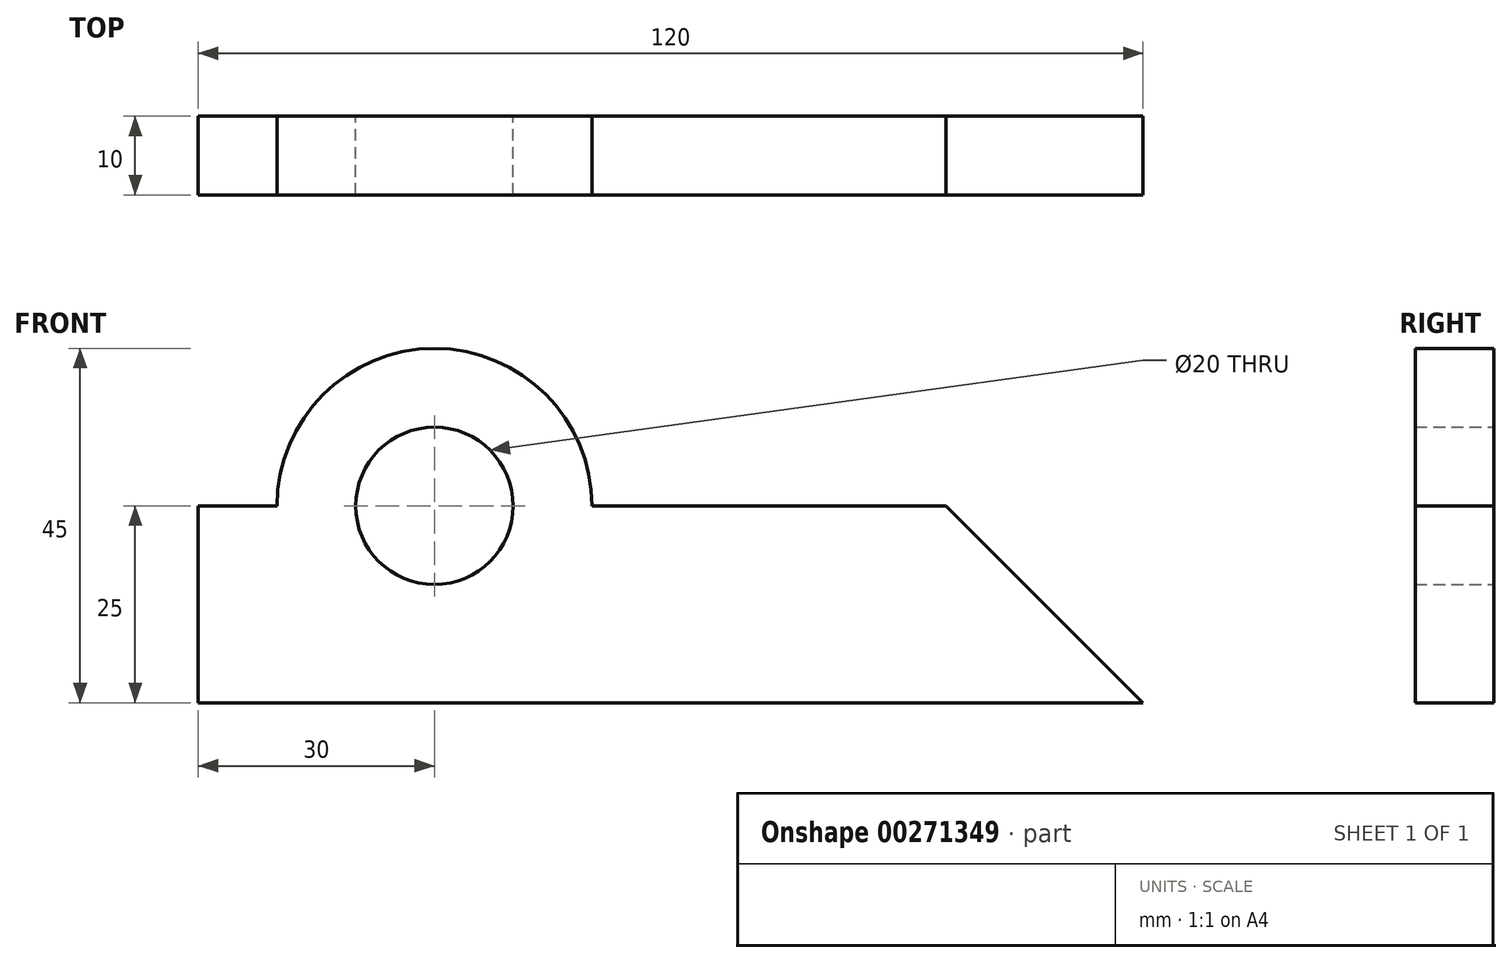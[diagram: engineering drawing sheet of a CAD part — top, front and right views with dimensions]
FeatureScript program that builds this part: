
annotation { "Feature Type Name" : "Feature", "Feature Type Description" : "" }
export const myFeature = defineFeature(function(context is Context, id is Id, definition is map)
    precondition{}
    {
        {
            var Q0;
            Q0=qCreatedBy(makeId("Front.planeOp"),FACE);
            var sketch = newSketch(context, id + "F0", { "sketchPlane" : qUnion([Q0])});
            skLineSegment(sketch, "E0", {"start": v(0, 0) * mm, "end": v(0, 25) * mm});
            skLineSegment(sketch, "E1", {"start": v(0, 25) * mm, "end": v(10, 25) * mm});
            skLineSegment(sketch, "E2", {"start": v(0, 0) * mm, "end": v(120, 0) * mm});
            skLineSegment(sketch, "E3", {"start": v(120, 0) * mm, "end": v(95, 25) * mm});
            skLineSegment(sketch, "E4", {"start": v(95, 25) * mm, "end": v(50, 25) * mm});
            skCircle(sketch, "E5", {"center": v(30, 25) * mm, "radius": 10 * mm});
            skArc(sketch, "E6", {"start": v(50, 25) * mm, "mid": v(30, 45) * mm, "end": v(10, 25) * mm});
            skSolve(sketch);
        }
        {
            var Q0;
            Q0=makeQuery(id+"F0.imprint","IMPRINT",FACE,{"disambiguationData":[TD([[makeQuery(id+"F0.imprint","IMPRINT",EDGE,{"derivedFrom":sQuery(id+"F0.wireOp",EDGE,"E0")}),-1.0]])]});
            extrude(context, id + "F1", {"entities" : qUnion([Q0]), "depth" : 10 * mm});
        }
    });
